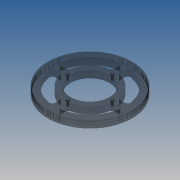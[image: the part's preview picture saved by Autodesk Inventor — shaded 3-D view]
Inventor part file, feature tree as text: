
AUTODESK INVENTOR PART (.ipt)
format: ipt  version: 2013 (Build 170138000, 138)  size: 1,248,768 bytes
history: native  units: mm
features: extrude x7, sketch x7, pattern_circular x3, mirror x1, chamfer x1, fillet x1
ambient origin geometry x8: Origin, YZ Plane, XZ Plane, XY Plane, X Axis, Y Axis, Z Axis, Center Point
bodies: Solid2 (feature_tree)
feature tree (20):
  extrude  "Extrusion11"  Depth=10.0mm
  extrude  "Extrusion12"  Depth=3.5mm
  pattern_circular  "Circular Pattern4"  Count=235  [1 undecoded]
  extrude  "Extrusion16"  Depth=1.0mm
  mirror  "Mirror2"
  chamfer  "Chamfer3"  Distance=2.5mm
  extrude  "Extrusion17"  Depth=1.0mm TaperAngle=45.0deg
  extrude  "Extrusion8"  Depth=12.0mm
  pattern_circular  "Circular Pattern5"  Count=7  [1 undecoded]
  fillet  "Fillet2"  Radius=10.0mm
  extrude  "Extrusion18"  Depth=2.5mm TaperAngle=0.0deg
  extrude  "Extrusion19"  Depth=40.0mm TaperAngle=360.0deg
  pattern_circular  "Circular Pattern6"  [2 undecoded]
  sketch  "Sketch8"  dims[d11=0.254mm d60=10.0mm]
  sketch  "Sketch9"  dims[d62=10.0mm d63=0.0mm d69=3.5mm]
  sketch  "Sketch11"  dims[d78=149.097647mm]
  sketch  "Sketch12"  dims[d80=8.0mm d81=0.0mm]
  sketch  "Sketch13"  dims[d82=1.59mm]
  sketch  "Sketch14"  dims[d84=8.0mm d85=0.0mm d86=2350.0mm]
  sketch  "Sketch15"  dims[d87=360.0deg d96=1.0mm d97=2.5mm d98=0.0mm d99=1.0mm d100=2.0mm d101=45.0deg d102=12.0mm d103=70.0mm d104=10.0mm d105=2.5mm d106=0.0mm d107=40.0mm d108=360.0deg d110=5.0mm d111=40.0mm d112=2.5mm d113=0.0mm d114=5.5mm d115=4.0mm d116=0.0mm d117=40.0mm d118=360.0deg]
note: 4 required parameter values undecoded (feature->parameter linkage not recoverable at this tier; creation-order binding heuristic only, values carry confidence <= 0.55)
